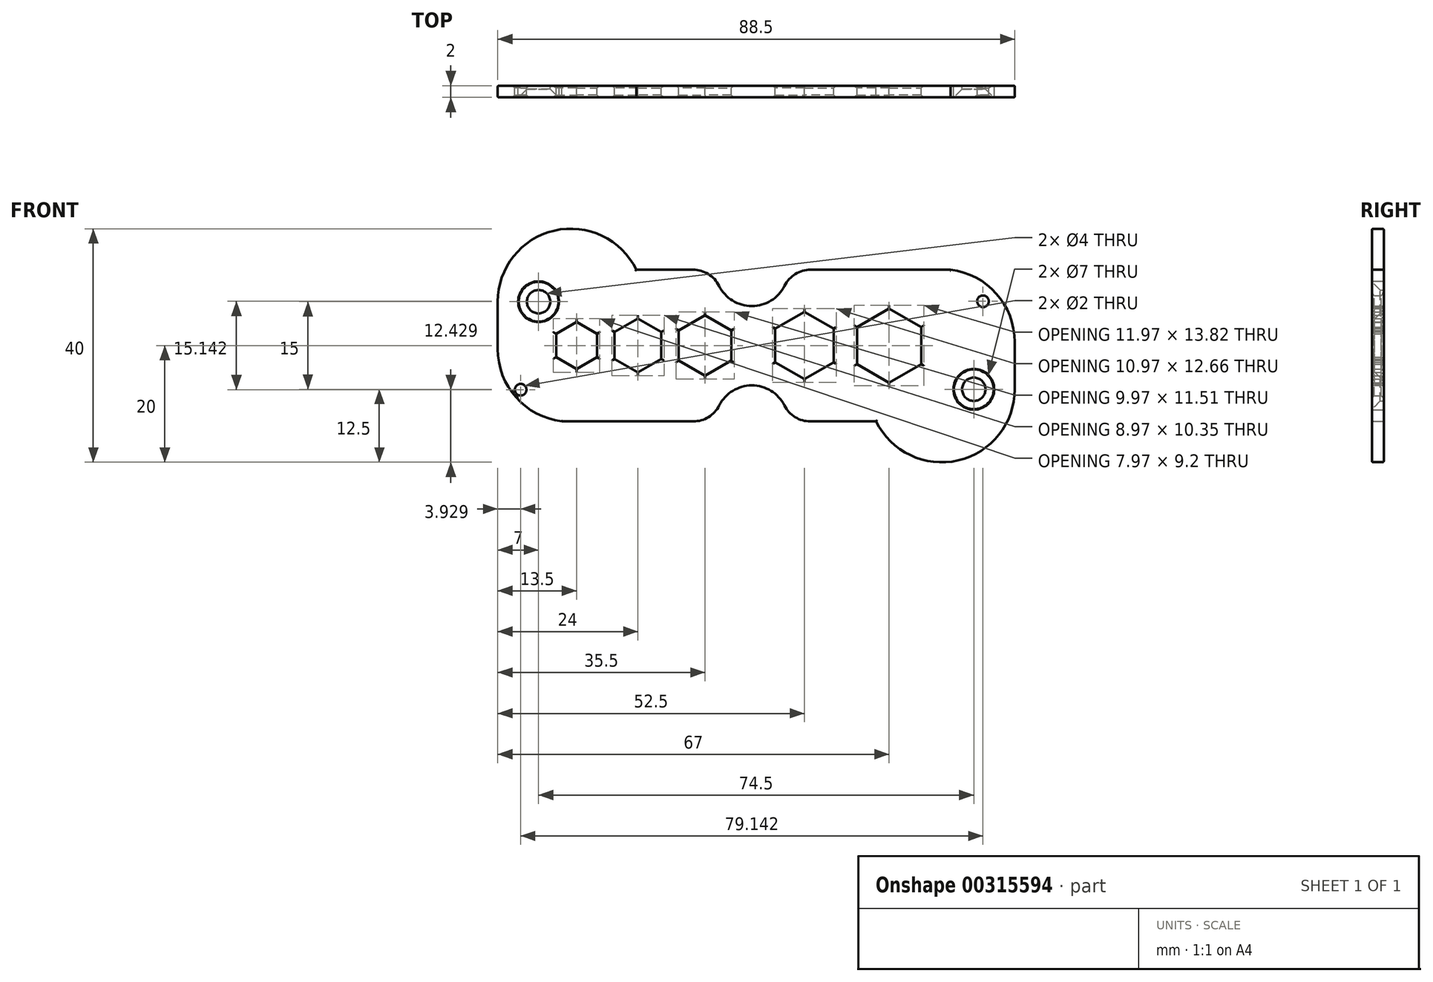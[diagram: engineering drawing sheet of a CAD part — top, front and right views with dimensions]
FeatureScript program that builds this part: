
annotation { "Feature Type Name" : "Feature", "Feature Type Description" : "" }
export const myFeature = defineFeature(function(context is Context, id is Id, definition is map)
    precondition{}
    {
        {
            var Q0;
            Q0=qCreatedBy(makeId("Front.planeOp"),FACE);
            var sketch = newSketch(context, id + "F0", { "sketchPlane" : qUnion([Q0])});
            skLineSegment(sketch, "E0", {"start": v(45, 0) * mm, "end": v(45, 0.6) * mm});
            skLineSegment(sketch, "E1", {"start": v(-43.5, 0) * mm, "end": v(-43.5, -0.6) * mm});
            skLineSegment(sketch, "E2", {"start": v(-43.5, 0) * mm, "end": v(-43.5, 7.5) * mm});
            skLineSegment(sketch, "E3", {"start": v(45, 0) * mm, "end": v(45, -7.5) * mm});
            skArc(sketch, "E4", {"start": v(-19.78, 13) * mm, "mid": v(-33.82, 19.68) * mm, "end": v(-43.5, 7.5) * mm});
            skArc(sketch, "E5", {"start": v(21.28, -13) * mm, "mid": v(35.32, -19.68) * mm, "end": v(45, -7.5) * mm});
            skPoint(sketch, "E6.visualSharp", {"position": v(45, 13) * mm});
            skArc(sketch, "E6.filletArc", {"start": v(45, 0.6) * mm, "mid": v(41.85, 8.88) * mm, "end": v(34, 13) * mm});
            skPoint(sketch, "E7.visualSharp", {"position": v(-43.5, -13) * mm});
            skArc(sketch, "E7.filletArc", {"start": v(-43.5, -0.6) * mm, "mid": v(-40.35, -8.88) * mm, "end": v(-32.5, -13) * mm});
            skCircle(sketch, "E8", {"center": v(-36.5, 7.5) * mm, "radius": 2 * mm});
            skCircle(sketch, "E9", {"center": v(38, -7.5) * mm, "radius": 2 * mm});
            skCircle(sketch, "E10", {"center": v(-39.57, -7.57) * mm, "radius": 1 * mm});
            skCircle(sketch, "E11", {"center": v(39.57, 7.57) * mm, "radius": 1 * mm});
            skArc(sketch, "E12", {"start": v(-5.6, 10.22) * mm, "mid": v(0, 6.74) * mm, "end": v(5.6, 10.22) * mm});
            skArc(sketch, "E13", {"start": v(5.57, -10.26) * mm, "mid": v(0, -6.84) * mm, "end": v(-5.58, -10.26) * mm});
            skLineSegment(sketch, "E14", {"start": v(-19.78, 13) * mm, "end": v(-10.08, 13) * mm});
            skLineSegment(sketch, "E15", {"start": v(10.08, 13) * mm, "end": v(34, 13) * mm});
            skLineSegment(sketch, "E16", {"start": v(-32.5, -13) * mm, "end": v(-10.04, -13) * mm});
            skLineSegment(sketch, "E17", {"start": v(10.03, -13) * mm, "end": v(21.28, -13) * mm});
            skArc(sketch, "E18.filletArc", {"start": v(10.08, 13) * mm, "mid": v(7.44, 12.25) * mm, "end": v(5.6, 10.22) * mm});
            skArc(sketch, "E19.filletArc", {"start": v(-5.6, 10.22) * mm, "mid": v(-7.44, 12.25) * mm, "end": v(-10.08, 13) * mm});
            skArc(sketch, "E20.filletArc", {"start": v(-10.04, -13) * mm, "mid": v(-7.42, -12.26) * mm, "end": v(-5.58, -10.26) * mm});
            skArc(sketch, "E21.filletArc", {"start": v(5.57, -10.26) * mm, "mid": v(7.42, -12.26) * mm, "end": v(10.03, -13) * mm});
            skCircle(sketch, "E22", {"center": v(-36.5, 7.5) * mm, "radius": 3.5 * mm});
            skCircle(sketch, "E23", {"center": v(38, -7.5) * mm, "radius": 3.5 * mm});
            skCircle(sketch, "E24.cCircle", {"center": v(-30, 0) * mm, "radius": 3.5 * mm, "construction": true});
            skLineSegment(sketch, "E24.0", {"start": v(-26.5, 2.02) * mm, "end": v(-26.5, -2.02) * mm});
            skLineSegment(sketch, "E24.1", {"start": v(-26.5, -2.02) * mm, "end": v(-30, -4.04) * mm});
            skLineSegment(sketch, "E24.2", {"start": v(-30, -4.04) * mm, "end": v(-33.5, -2.02) * mm});
            skLineSegment(sketch, "E24.3", {"start": v(-33.5, -2.02) * mm, "end": v(-33.5, 2.02) * mm});
            skLineSegment(sketch, "E24.4", {"start": v(-33.5, 2.02) * mm, "end": v(-30, 4.04) * mm});
            skLineSegment(sketch, "E24.5", {"start": v(-30, 4.04) * mm, "end": v(-26.5, 2.02) * mm});
            skPoint(sketch, "E24.0.midPoint", {"position": v(-26.5, 0) * mm});
            skCircle(sketch, "E25.cCircle", {"center": v(-19.5, 0) * mm, "radius": 4 * mm, "construction": true});
            skLineSegment(sketch, "E25.0", {"start": v(-15.5, 2.3) * mm, "end": v(-15.5, -2.3) * mm});
            skLineSegment(sketch, "E25.1", {"start": v(-15.5, -2.3) * mm, "end": v(-19.5, -4.62) * mm});
            skLineSegment(sketch, "E25.2", {"start": v(-19.5, -4.62) * mm, "end": v(-23.5, -2.3) * mm});
            skLineSegment(sketch, "E25.3", {"start": v(-23.5, -2.3) * mm, "end": v(-23.5, 2.3) * mm});
            skLineSegment(sketch, "E25.4", {"start": v(-23.5, 2.3) * mm, "end": v(-19.5, 4.62) * mm});
            skLineSegment(sketch, "E25.5", {"start": v(-19.5, 4.62) * mm, "end": v(-15.5, 2.3) * mm});
            skPoint(sketch, "E25.0.midPoint", {"position": v(-15.5, 0) * mm});
            skCircle(sketch, "E26.cCircle", {"center": v(-8, 0) * mm, "radius": 4.5 * mm, "construction": true});
            skLineSegment(sketch, "E26.0", {"start": v(-12.5, -2.6) * mm, "end": v(-12.5, 2.6) * mm});
            skLineSegment(sketch, "E26.1", {"start": v(-12.5, 2.6) * mm, "end": v(-8, 5.2) * mm});
            skLineSegment(sketch, "E26.2", {"start": v(-8, 5.2) * mm, "end": v(-3.5, 2.6) * mm});
            skLineSegment(sketch, "E26.3", {"start": v(-3.5, 2.6) * mm, "end": v(-3.5, -2.6) * mm});
            skLineSegment(sketch, "E26.4", {"start": v(-3.5, -2.6) * mm, "end": v(-8, -5.2) * mm});
            skLineSegment(sketch, "E26.5", {"start": v(-8, -5.2) * mm, "end": v(-12.5, -2.6) * mm});
            skPoint(sketch, "E26.0.midPoint", {"position": v(-12.5, 0) * mm});
            skCircle(sketch, "E27.cCircle", {"center": v(9, 0) * mm, "radius": 5 * mm, "construction": true});
            skLineSegment(sketch, "E27.0", {"start": v(4, -2.89) * mm, "end": v(4, 2.89) * mm});
            skLineSegment(sketch, "E27.1", {"start": v(4, 2.89) * mm, "end": v(9, 5.77) * mm});
            skLineSegment(sketch, "E27.2", {"start": v(9, 5.77) * mm, "end": v(14, 2.89) * mm});
            skLineSegment(sketch, "E27.3", {"start": v(14, 2.89) * mm, "end": v(14, -2.89) * mm});
            skLineSegment(sketch, "E27.4", {"start": v(14, -2.89) * mm, "end": v(9, -5.77) * mm});
            skLineSegment(sketch, "E27.5", {"start": v(9, -5.77) * mm, "end": v(4, -2.89) * mm});
            skPoint(sketch, "E27.0.midPoint", {"position": v(4, 0) * mm});
            skPoint(sketch, "E28.endSnap0", {"position": v(14, 0) * mm});
            skCircle(sketch, "E29.cCircle", {"center": v(23.5, 0) * mm, "radius": 5.5 * mm, "construction": true});
            skLineSegment(sketch, "E29.0", {"start": v(18, -3.18) * mm, "end": v(18, 3.18) * mm});
            skLineSegment(sketch, "E29.1", {"start": v(18, 3.18) * mm, "end": v(23.5, 6.35) * mm});
            skLineSegment(sketch, "E29.2", {"start": v(23.5, 6.35) * mm, "end": v(29, 3.18) * mm});
            skLineSegment(sketch, "E29.3", {"start": v(29, 3.18) * mm, "end": v(29, -3.18) * mm});
            skLineSegment(sketch, "E29.4", {"start": v(29, -3.18) * mm, "end": v(23.5, -6.35) * mm});
            skLineSegment(sketch, "E29.5", {"start": v(23.5, -6.35) * mm, "end": v(18, -3.18) * mm});
            skPoint(sketch, "E29.0.midPoint", {"position": v(18, 0) * mm});
            skLineSegment(sketch, "E30", {"start": v(-40, 7.5) * mm, "end": v(-38.5, 7.5) * mm});
            skSolve(sketch);
        }
        {
            var Q0;
            Q0=makeQuery(id+"F0.imprint","IMPRINT",FACE,{"disambiguationData":[TD([[makeQuery(id+"F0.imprint","IMPRINT",EDGE,{"derivedFrom":sQuery(id+"F0.wireOp",EDGE,"E8")}),-1.0]])]});
            extrude(context, id + "F1", {"entities" : qUnion([Q0]), "depth" : 2 * mm});
        }
        {
            var Q0;
            Q0=makeQuery(id+"F1.opExtrude","CAP_EDGE",EDGE,{"disambiguationData":[OSD([sQuery(id+"F0.wireOp",EDGE,"E8")])],"isStart":false});
            chamfer(context, id + "F2", {"entities" : qUnion([Q0]), "width" : 1.4 * mm, "tangentPropagation" : true});
        }
        {
            var Q0;
            Q0=makeQuery(id+"F0.imprint","IMPRINT",FACE,{"disambiguationData":[TD([[makeQuery(id+"F0.imprint","IMPRINT",EDGE,{"derivedFrom":sQuery(id+"F0.wireOp",EDGE,"E9")}),-1.0]])]});
            extrude(context, id + "F3", {"entities" : qUnion([Q0]), "depth" : 2 * mm});
        }
        {
            var Q0;
            Q0=makeQuery(id+"F3.opExtrude","CAP_EDGE",EDGE,{"disambiguationData":[OSD([sQuery(id+"F0.wireOp",EDGE,"E9")])],"isStart":false});
            chamfer(context, id + "F4", {"entities" : qUnion([Q0]), "width" : 1.4 * mm, "tangentPropagation" : true});
        }
        {
            var Q0;
            Q0=makeQuery(id+"F0.imprint","IMPRINT",FACE,{"disambiguationData":[TD([[makeQuery(id+"F0.imprint","IMPRINT",EDGE,{"derivedFrom":sQuery(id+"F0.wireOp",EDGE,"E0")}),1.0]])]});
            extrude(context, id + "F5", {"entities" : qUnion([Q0]), "depth" : 2 * mm});
        }
        {
            var Q0;
            Q0=makeQuery(id+"F5.opExtrude","CAP_EDGE",EDGE,{"disambiguationData":[OSD([sQuery(id+"F0.wireOp",EDGE,"E24.5")])],"isStart":false});
            var Q1;
            Q1=makeQuery(id+"F5.opExtrude","CAP_EDGE",EDGE,{"disambiguationData":[OSD([sQuery(id+"F0.wireOp",EDGE,"E24.4")])],"isStart":false});
            var Q2;
            Q2=makeQuery(id+"F5.opExtrude","CAP_EDGE",EDGE,{"disambiguationData":[OSD([sQuery(id+"F0.wireOp",EDGE,"E24.3")])],"isStart":false});
            var Q3;
            Q3=makeQuery(id+"F5.opExtrude","CAP_EDGE",EDGE,{"disambiguationData":[OSD([sQuery(id+"F0.wireOp",EDGE,"E24.2")])],"isStart":false});
            var Q4;
            Q4=makeQuery(id+"F5.opExtrude","CAP_EDGE",EDGE,{"disambiguationData":[OSD([sQuery(id+"F0.wireOp",EDGE,"E24.1")])],"isStart":false});
            var Q5;
            Q5=makeQuery(id+"F5.opExtrude","CAP_EDGE",EDGE,{"disambiguationData":[OSD([sQuery(id+"F0.wireOp",EDGE,"E24.0")])],"isStart":false});
            var Q6;
            Q6=makeQuery(id+"F5.opExtrude","CAP_EDGE",EDGE,{"disambiguationData":[OSD([sQuery(id+"F0.wireOp",EDGE,"E25.4")])],"isStart":false});
            var Q7;
            Q7=makeQuery(id+"F5.opExtrude","CAP_EDGE",EDGE,{"disambiguationData":[OSD([sQuery(id+"F0.wireOp",EDGE,"E25.5")])],"isStart":false});
            var Q8;
            Q8=makeQuery(id+"F5.opExtrude","CAP_EDGE",EDGE,{"disambiguationData":[OSD([sQuery(id+"F0.wireOp",EDGE,"E25.0")])],"isStart":false});
            var Q9;
            Q9=makeQuery(id+"F5.opExtrude","CAP_EDGE",EDGE,{"disambiguationData":[OSD([sQuery(id+"F0.wireOp",EDGE,"E25.1")])],"isStart":false});
            var Q10;
            Q10=makeQuery(id+"F5.opExtrude","CAP_EDGE",EDGE,{"disambiguationData":[OSD([sQuery(id+"F0.wireOp",EDGE,"E25.2")])],"isStart":false});
            var Q11;
            Q11=makeQuery(id+"F5.opExtrude","CAP_EDGE",EDGE,{"disambiguationData":[OSD([sQuery(id+"F0.wireOp",EDGE,"E25.3")])],"isStart":false});
            var Q12;
            Q12=makeQuery(id+"F5.opExtrude","CAP_EDGE",EDGE,{"disambiguationData":[OSD([sQuery(id+"F0.wireOp",EDGE,"E26.1")])],"isStart":false});
            var Q13;
            Q13=makeQuery(id+"F5.opExtrude","CAP_EDGE",EDGE,{"disambiguationData":[OSD([sQuery(id+"F0.wireOp",EDGE,"E26.2")])],"isStart":false});
            var Q14;
            Q14=makeQuery(id+"F5.opExtrude","CAP_EDGE",EDGE,{"disambiguationData":[OSD([sQuery(id+"F0.wireOp",EDGE,"E26.3")])],"isStart":false});
            var Q15;
            Q15=makeQuery(id+"F5.opExtrude","CAP_EDGE",EDGE,{"disambiguationData":[OSD([sQuery(id+"F0.wireOp",EDGE,"E26.4")])],"isStart":false});
            var Q16;
            Q16=makeQuery(id+"F5.opExtrude","CAP_EDGE",EDGE,{"disambiguationData":[OSD([sQuery(id+"F0.wireOp",EDGE,"E26.5")])],"isStart":false});
            var Q17;
            Q17=makeQuery(id+"F5.opExtrude","CAP_EDGE",EDGE,{"disambiguationData":[OSD([sQuery(id+"F0.wireOp",EDGE,"E26.0")])],"isStart":false});
            var Q18;
            Q18=makeQuery(id+"F5.opExtrude","CAP_EDGE",EDGE,{"disambiguationData":[OSD([sQuery(id+"F0.wireOp",EDGE,"E27.0")])],"isStart":false});
            var Q19;
            Q19=makeQuery(id+"F5.opExtrude","CAP_EDGE",EDGE,{"disambiguationData":[OSD([sQuery(id+"F0.wireOp",EDGE,"E27.1")])],"isStart":false});
            var Q20;
            Q20=makeQuery(id+"F5.opExtrude","CAP_EDGE",EDGE,{"disambiguationData":[OSD([sQuery(id+"F0.wireOp",EDGE,"E27.2")])],"isStart":false});
            var Q21;
            Q21=makeQuery(id+"F5.opExtrude","CAP_EDGE",EDGE,{"disambiguationData":[OSD([sQuery(id+"F0.wireOp",EDGE,"E27.3")])],"isStart":false});
            var Q22;
            Q22=makeQuery(id+"F5.opExtrude","CAP_EDGE",EDGE,{"disambiguationData":[OSD([sQuery(id+"F0.wireOp",EDGE,"E27.4")])],"isStart":false});
            var Q23;
            Q23=makeQuery(id+"F5.opExtrude","CAP_EDGE",EDGE,{"disambiguationData":[OSD([sQuery(id+"F0.wireOp",EDGE,"E27.5")])],"isStart":false});
            var Q24;
            Q24=makeQuery(id+"F5.opExtrude","CAP_EDGE",EDGE,{"disambiguationData":[OSD([sQuery(id+"F0.wireOp",EDGE,"E29.1")])],"isStart":false});
            var Q25;
            Q25=makeQuery(id+"F5.opExtrude","CAP_EDGE",EDGE,{"disambiguationData":[OSD([sQuery(id+"F0.wireOp",EDGE,"E29.2")])],"isStart":false});
            var Q26;
            Q26=makeQuery(id+"F5.opExtrude","CAP_EDGE",EDGE,{"disambiguationData":[OSD([sQuery(id+"F0.wireOp",EDGE,"E29.3")])],"isStart":false});
            var Q27;
            Q27=makeQuery(id+"F5.opExtrude","CAP_EDGE",EDGE,{"disambiguationData":[OSD([sQuery(id+"F0.wireOp",EDGE,"E29.4")])],"isStart":false});
            var Q28;
            Q28=makeQuery(id+"F5.opExtrude","CAP_EDGE",EDGE,{"disambiguationData":[OSD([sQuery(id+"F0.wireOp",EDGE,"E29.5")])],"isStart":false});
            var Q29;
            Q29=makeQuery(id+"F5.opExtrude","CAP_EDGE",EDGE,{"disambiguationData":[OSD([sQuery(id+"F0.wireOp",EDGE,"E29.0")])],"isStart":false});
            var Q30;
            Q30=makeQuery(id+"F5.opExtrude","CAP_EDGE",EDGE,{"disambiguationData":[OSD([sQuery(id+"F0.wireOp",EDGE,"E10")])],"isStart":false});
            var Q31;
            Q31=makeQuery(id+"F5.opExtrude","CAP_EDGE",EDGE,{"disambiguationData":[OSD([sQuery(id+"F0.wireOp",EDGE,"E11")])],"isStart":false});
            var Q32;
            Q32=makeQuery(id+"F5.opExtrude","CAP_EDGE",EDGE,{"disambiguationData":[OSD([sQuery(id+"F0.wireOp",EDGE,"E29.0")])],"isStart":true});
            var Q33;
            Q33=makeQuery(id+"F5.opExtrude","CAP_EDGE",EDGE,{"disambiguationData":[OSD([sQuery(id+"F0.wireOp",EDGE,"E29.1")])],"isStart":true});
            var Q34;
            Q34=makeQuery(id+"F5.opExtrude","CAP_EDGE",EDGE,{"disambiguationData":[OSD([sQuery(id+"F0.wireOp",EDGE,"E29.2")])],"isStart":true});
            var Q35;
            Q35=makeQuery(id+"F5.opExtrude","CAP_EDGE",EDGE,{"disambiguationData":[OSD([sQuery(id+"F0.wireOp",EDGE,"E29.3")])],"isStart":true});
            var Q36;
            Q36=makeQuery(id+"F5.opExtrude","CAP_EDGE",EDGE,{"disambiguationData":[OSD([sQuery(id+"F0.wireOp",EDGE,"E29.4")])],"isStart":true});
            var Q37;
            Q37=makeQuery(id+"F5.opExtrude","CAP_EDGE",EDGE,{"disambiguationData":[OSD([sQuery(id+"F0.wireOp",EDGE,"E29.5")])],"isStart":true});
            var Q38;
            Q38=makeQuery(id+"F5.opExtrude","CAP_EDGE",EDGE,{"disambiguationData":[OSD([sQuery(id+"F0.wireOp",EDGE,"E27.3")])],"isStart":true});
            var Q39;
            Q39=makeQuery(id+"F5.opExtrude","CAP_EDGE",EDGE,{"disambiguationData":[OSD([sQuery(id+"F0.wireOp",EDGE,"E27.2")])],"isStart":true});
            var Q40;
            Q40=makeQuery(id+"F5.opExtrude","CAP_EDGE",EDGE,{"disambiguationData":[OSD([sQuery(id+"F0.wireOp",EDGE,"E27.1")])],"isStart":true});
            var Q41;
            Q41=makeQuery(id+"F5.opExtrude","CAP_EDGE",EDGE,{"disambiguationData":[OSD([sQuery(id+"F0.wireOp",EDGE,"E27.0")])],"isStart":true});
            var Q42;
            Q42=makeQuery(id+"F5.opExtrude","CAP_EDGE",EDGE,{"disambiguationData":[OSD([sQuery(id+"F0.wireOp",EDGE,"E27.5")])],"isStart":true});
            var Q43;
            Q43=makeQuery(id+"F5.opExtrude","CAP_EDGE",EDGE,{"disambiguationData":[OSD([sQuery(id+"F0.wireOp",EDGE,"E27.4")])],"isStart":true});
            var Q44;
            Q44=makeQuery(id+"F5.opExtrude","CAP_EDGE",EDGE,{"disambiguationData":[OSD([sQuery(id+"F0.wireOp",EDGE,"E26.2")])],"isStart":true});
            var Q45;
            Q45=makeQuery(id+"F5.opExtrude","CAP_EDGE",EDGE,{"disambiguationData":[OSD([sQuery(id+"F0.wireOp",EDGE,"E26.1")])],"isStart":true});
            var Q46;
            Q46=makeQuery(id+"F5.opExtrude","CAP_EDGE",EDGE,{"disambiguationData":[OSD([sQuery(id+"F0.wireOp",EDGE,"E26.0")])],"isStart":true});
            var Q47;
            Q47=makeQuery(id+"F5.opExtrude","CAP_EDGE",EDGE,{"disambiguationData":[OSD([sQuery(id+"F0.wireOp",EDGE,"E26.5")])],"isStart":true});
            var Q48;
            Q48=makeQuery(id+"F5.opExtrude","CAP_EDGE",EDGE,{"disambiguationData":[OSD([sQuery(id+"F0.wireOp",EDGE,"E26.4")])],"isStart":true});
            var Q49;
            Q49=makeQuery(id+"F5.opExtrude","CAP_EDGE",EDGE,{"disambiguationData":[OSD([sQuery(id+"F0.wireOp",EDGE,"E26.3")])],"isStart":true});
            var Q50;
            Q50=makeQuery(id+"F5.opExtrude","CAP_EDGE",EDGE,{"disambiguationData":[OSD([sQuery(id+"F0.wireOp",EDGE,"E25.5")])],"isStart":true});
            var Q51;
            Q51=makeQuery(id+"F5.opExtrude","CAP_EDGE",EDGE,{"disambiguationData":[OSD([sQuery(id+"F0.wireOp",EDGE,"E25.4")])],"isStart":true});
            var Q52;
            Q52=makeQuery(id+"F5.opExtrude","CAP_EDGE",EDGE,{"disambiguationData":[OSD([sQuery(id+"F0.wireOp",EDGE,"E25.3")])],"isStart":true});
            var Q53;
            Q53=makeQuery(id+"F5.opExtrude","CAP_EDGE",EDGE,{"disambiguationData":[OSD([sQuery(id+"F0.wireOp",EDGE,"E25.2")])],"isStart":true});
            var Q54;
            Q54=makeQuery(id+"F5.opExtrude","CAP_EDGE",EDGE,{"disambiguationData":[OSD([sQuery(id+"F0.wireOp",EDGE,"E25.1")])],"isStart":true});
            var Q55;
            Q55=makeQuery(id+"F5.opExtrude","CAP_EDGE",EDGE,{"disambiguationData":[OSD([sQuery(id+"F0.wireOp",EDGE,"E25.0")])],"isStart":true});
            var Q56;
            Q56=makeQuery(id+"F5.opExtrude","CAP_EDGE",EDGE,{"disambiguationData":[OSD([sQuery(id+"F0.wireOp",EDGE,"E24.5")])],"isStart":true});
            var Q57;
            Q57=makeQuery(id+"F5.opExtrude","CAP_EDGE",EDGE,{"disambiguationData":[OSD([sQuery(id+"F0.wireOp",EDGE,"E24.4")])],"isStart":true});
            var Q58;
            Q58=makeQuery(id+"F5.opExtrude","CAP_EDGE",EDGE,{"disambiguationData":[OSD([sQuery(id+"F0.wireOp",EDGE,"E24.3")])],"isStart":true});
            var Q59;
            Q59=makeQuery(id+"F5.opExtrude","CAP_EDGE",EDGE,{"disambiguationData":[OSD([sQuery(id+"F0.wireOp",EDGE,"E24.2")])],"isStart":true});
            var Q60;
            Q60=makeQuery(id+"F5.opExtrude","CAP_EDGE",EDGE,{"disambiguationData":[OSD([sQuery(id+"F0.wireOp",EDGE,"E24.1")])],"isStart":true});
            var Q61;
            Q61=makeQuery(id+"F5.opExtrude","CAP_EDGE",EDGE,{"disambiguationData":[OSD([sQuery(id+"F0.wireOp",EDGE,"E24.0")])],"isStart":true});
            var Q62;
            Q62=makeQuery(id+"F5.opExtrude","CAP_EDGE",EDGE,{"disambiguationData":[OSD([sQuery(id+"F0.wireOp",EDGE,"E11")])],"isStart":true});
            var Q63;
            Q63=makeQuery(id+"F5.opExtrude","CAP_EDGE",EDGE,{"disambiguationData":[OSD([sQuery(id+"F0.wireOp",EDGE,"E10")])],"isStart":true});
            chamfer(context, id + "F6", {"entities" : qUnion([Q0, Q1, Q2, Q3, Q4, Q5, Q6, Q7, Q8, Q9, Q10, Q11, Q12, Q13, Q14, Q15, Q16, Q17, Q18, Q19, Q20, Q21, Q22, Q23, Q24, Q25, Q26, Q27, Q28, Q29, Q30, Q31, Q32, Q33, Q34, Q35, Q36, Q37, Q38, Q39, Q40, Q41, Q42, Q43, Q44, Q45, Q46, Q47, Q48, Q49, Q50, Q51, Q52, Q53, Q54, Q55, Q56, Q57, Q58, Q59, Q60, Q61, Q62, Q63]), "width" : 0.4 * mm, "tangentPropagation" : true});
        }
        {
            var Q0;
            Q0=makeQuery(id+"F5.opExtrude","CAP_FACE",FACE,{"disambiguationData":[OSD([sQuery(id+"F0.wireOp",EDGE,"E0"),sQuery(id+"F0.wireOp",EDGE,"E1"),sQuery(id+"F0.wireOp",EDGE,"E2"),sQuery(id+"F0.wireOp",EDGE,"E3"),sQuery(id+"F0.wireOp",EDGE,"E4"),sQuery(id+"F0.wireOp",EDGE,"E5"),sQuery(id+"F0.wireOp",EDGE,"E6.filletArc"),sQuery(id+"F0.wireOp",EDGE,"E7.filletArc"),sQuery(id+"F0.wireOp",EDGE,"E10"),sQuery(id+"F0.wireOp",EDGE,"E11"),sQuery(id+"F0.wireOp",EDGE,"E12"),sQuery(id+"F0.wireOp",EDGE,"E13"),sQuery(id+"F0.wireOp",EDGE,"E14"),sQuery(id+"F0.wireOp",EDGE,"E15"),sQuery(id+"F0.wireOp",EDGE,"E16"),sQuery(id+"F0.wireOp",EDGE,"E17"),sQuery(id+"F0.wireOp",EDGE,"E18.filletArc"),sQuery(id+"F0.wireOp",EDGE,"E19.filletArc"),sQuery(id+"F0.wireOp",EDGE,"E20.filletArc"),sQuery(id+"F0.wireOp",EDGE,"E21.filletArc"),sQuery(id+"F0.wireOp",EDGE,"E22"),sQuery(id+"F0.wireOp",EDGE,"E23"),sQuery(id+"F0.wireOp",EDGE,"E24.0"),sQuery(id+"F0.wireOp",EDGE,"E24.1"),sQuery(id+"F0.wireOp",EDGE,"E24.2"),sQuery(id+"F0.wireOp",EDGE,"E24.3"),sQuery(id+"F0.wireOp",EDGE,"E24.4"),sQuery(id+"F0.wireOp",EDGE,"E24.5"),sQuery(id+"F0.wireOp",EDGE,"E25.0"),sQuery(id+"F0.wireOp",EDGE,"E25.1"),sQuery(id+"F0.wireOp",EDGE,"E25.2"),sQuery(id+"F0.wireOp",EDGE,"E25.3"),sQuery(id+"F0.wireOp",EDGE,"E25.4"),sQuery(id+"F0.wireOp",EDGE,"E25.5"),sQuery(id+"F0.wireOp",EDGE,"E26.0"),sQuery(id+"F0.wireOp",EDGE,"E26.1"),sQuery(id+"F0.wireOp",EDGE,"E26.2"),sQuery(id+"F0.wireOp",EDGE,"E26.3"),sQuery(id+"F0.wireOp",EDGE,"E26.4"),sQuery(id+"F0.wireOp",EDGE,"E26.5"),sQuery(id+"F0.wireOp",EDGE,"E27.0"),sQuery(id+"F0.wireOp",EDGE,"E27.1"),sQuery(id+"F0.wireOp",EDGE,"E27.2"),sQuery(id+"F0.wireOp",EDGE,"E27.3"),sQuery(id+"F0.wireOp",EDGE,"E27.4"),sQuery(id+"F0.wireOp",EDGE,"E27.5"),sQuery(id+"F0.wireOp",EDGE,"E29.0"),sQuery(id+"F0.wireOp",EDGE,"E29.1"),sQuery(id+"F0.wireOp",EDGE,"E29.2"),sQuery(id+"F0.wireOp",EDGE,"E29.3"),sQuery(id+"F0.wireOp",EDGE,"E29.4"),sQuery(id+"F0.wireOp",EDGE,"E29.5")])],"isStart":true});
            var Q1;
            Q1=makeQuery(id+"F5.opExtrude","CAP_FACE",FACE,{"disambiguationData":[OSD([sQuery(id+"F0.wireOp",EDGE,"E0"),sQuery(id+"F0.wireOp",EDGE,"E1"),sQuery(id+"F0.wireOp",EDGE,"E2"),sQuery(id+"F0.wireOp",EDGE,"E3"),sQuery(id+"F0.wireOp",EDGE,"E4"),sQuery(id+"F0.wireOp",EDGE,"E5"),sQuery(id+"F0.wireOp",EDGE,"E6.filletArc"),sQuery(id+"F0.wireOp",EDGE,"E7.filletArc"),sQuery(id+"F0.wireOp",EDGE,"E10"),sQuery(id+"F0.wireOp",EDGE,"E11"),sQuery(id+"F0.wireOp",EDGE,"E12"),sQuery(id+"F0.wireOp",EDGE,"E13"),sQuery(id+"F0.wireOp",EDGE,"E14"),sQuery(id+"F0.wireOp",EDGE,"E15"),sQuery(id+"F0.wireOp",EDGE,"E16"),sQuery(id+"F0.wireOp",EDGE,"E17"),sQuery(id+"F0.wireOp",EDGE,"E18.filletArc"),sQuery(id+"F0.wireOp",EDGE,"E19.filletArc"),sQuery(id+"F0.wireOp",EDGE,"E20.filletArc"),sQuery(id+"F0.wireOp",EDGE,"E21.filletArc"),sQuery(id+"F0.wireOp",EDGE,"E22"),sQuery(id+"F0.wireOp",EDGE,"E23"),sQuery(id+"F0.wireOp",EDGE,"E24.0"),sQuery(id+"F0.wireOp",EDGE,"E24.1"),sQuery(id+"F0.wireOp",EDGE,"E24.2"),sQuery(id+"F0.wireOp",EDGE,"E24.3"),sQuery(id+"F0.wireOp",EDGE,"E24.4"),sQuery(id+"F0.wireOp",EDGE,"E24.5"),sQuery(id+"F0.wireOp",EDGE,"E25.0"),sQuery(id+"F0.wireOp",EDGE,"E25.1"),sQuery(id+"F0.wireOp",EDGE,"E25.2"),sQuery(id+"F0.wireOp",EDGE,"E25.3"),sQuery(id+"F0.wireOp",EDGE,"E25.4"),sQuery(id+"F0.wireOp",EDGE,"E25.5"),sQuery(id+"F0.wireOp",EDGE,"E26.0"),sQuery(id+"F0.wireOp",EDGE,"E26.1"),sQuery(id+"F0.wireOp",EDGE,"E26.2"),sQuery(id+"F0.wireOp",EDGE,"E26.3"),sQuery(id+"F0.wireOp",EDGE,"E26.4"),sQuery(id+"F0.wireOp",EDGE,"E26.5"),sQuery(id+"F0.wireOp",EDGE,"E27.0"),sQuery(id+"F0.wireOp",EDGE,"E27.1"),sQuery(id+"F0.wireOp",EDGE,"E27.2"),sQuery(id+"F0.wireOp",EDGE,"E27.3"),sQuery(id+"F0.wireOp",EDGE,"E27.4"),sQuery(id+"F0.wireOp",EDGE,"E27.5"),sQuery(id+"F0.wireOp",EDGE,"E29.0"),sQuery(id+"F0.wireOp",EDGE,"E29.1"),sQuery(id+"F0.wireOp",EDGE,"E29.2"),sQuery(id+"F0.wireOp",EDGE,"E29.3"),sQuery(id+"F0.wireOp",EDGE,"E29.4"),sQuery(id+"F0.wireOp",EDGE,"E29.5")])],"isStart":false});
            fillet(context, id + "F7", {"entities" : qUnion([Q0, Q1]), "radius" : 0.2 * mm, "tangentPropagation" : true, "allowEdgeOverflow" : false});
        }
    });
